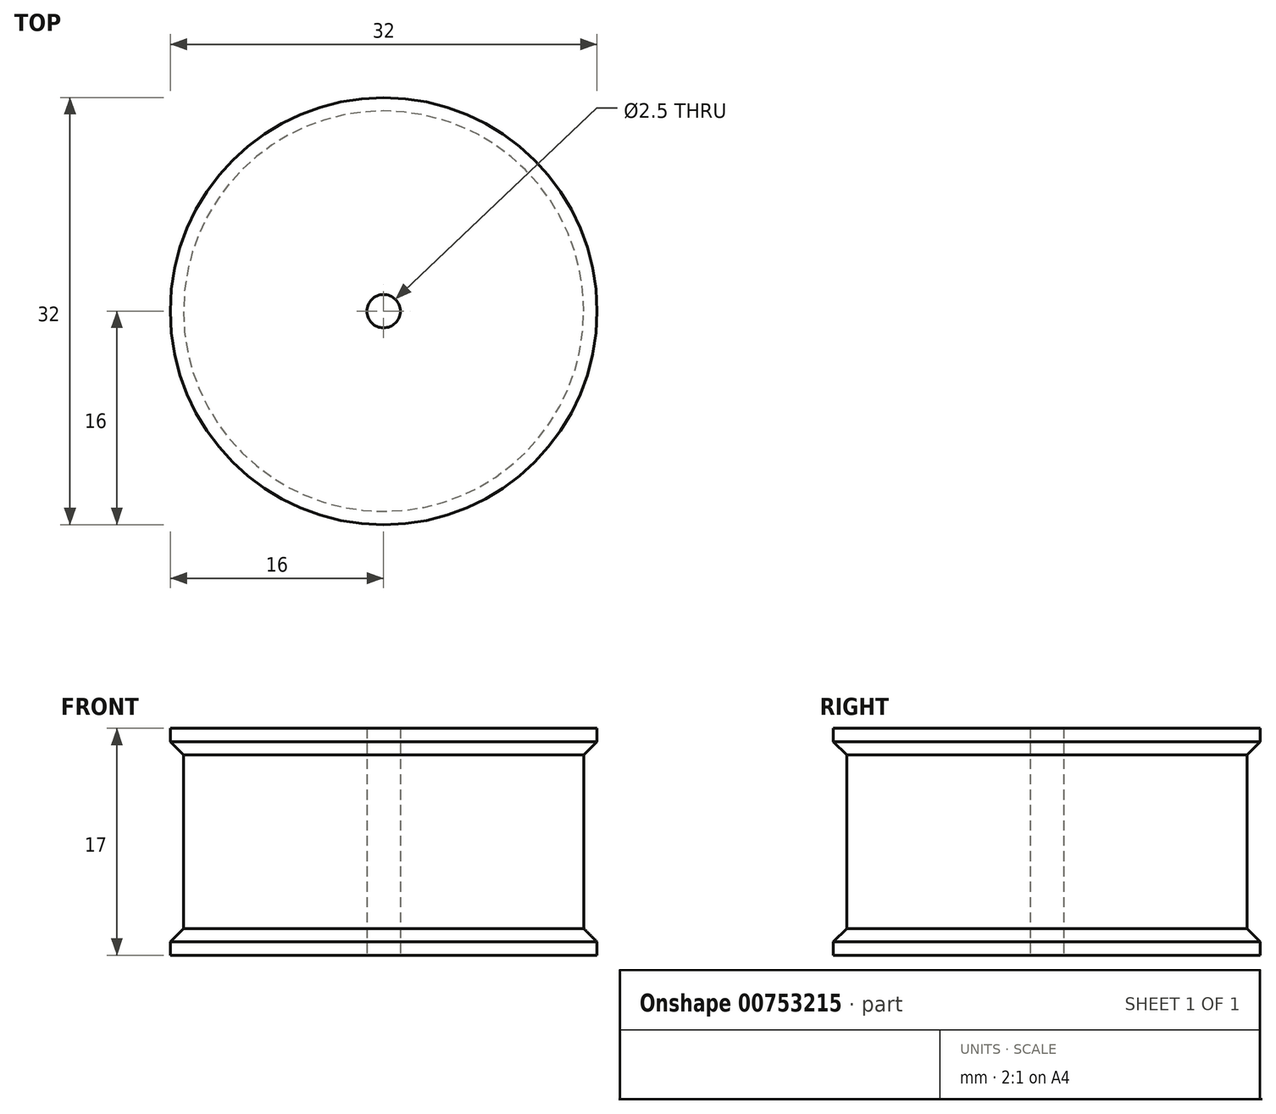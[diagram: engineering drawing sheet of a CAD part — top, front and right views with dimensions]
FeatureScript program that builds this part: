
annotation { "Feature Type Name" : "Feature", "Feature Type Description" : "" }
export const myFeature = defineFeature(function(context is Context, id is Id, definition is map)
    precondition{}
    {
        {
            var Q0;
            Q0=qCreatedBy(makeId("Top.planeOp"),FACE);
            var sketch = newSketch(context, id + "F0", { "sketchPlane" : qUnion([Q0])});
            skCircle(sketch, "E0", {"center": v(0, 0) * mm, "radius": 16 * mm});
            skSolve(sketch);
        }
        {
            var Q0;
            Q0 = qSketchRegion(id + "F0", true);
            extrude(context, id + "F1", {"entities" : qUnion([Q0]), "depth" : 2 * mm, "offsetDistance" : 25 * mm});
        }
        {
            var Q0;
            Q0=makeQuery(id+"F1.opExtrude","CAP_EDGE",EDGE,{"disambiguationData":[OSD([sQuery(id+"F0.wireOp",EDGE,"E0")])],"isStart":false});
            chamfer(context, id + "F2", {"entities" : qUnion([Q0]), "width" : 1 * mm, "tangentPropagation" : true});
        }
        {
            var Q0;
            Q0=qCreatedBy(makeId("Top.planeOp"),FACE);
            var sketch = newSketch(context, id + "F3", { "sketchPlane" : qUnion([Q0])});
            skCircle(sketch, "E1", {"center": v(0, 0) * mm, "radius": 15 * mm});
            skSolve(sketch);
        }
        {
            var Q0;
            Q0=makeQuery(id+"F1.opExtrude","CAP_FACE",FACE,{"disambiguationData":[OSD([sQuery(id+"F0.wireOp",EDGE,"E0")])],"isStart":false});
            var sketch = newSketch(context, id + "F4", { "sketchPlane" : qUnion([Q0])});
            skSolve(sketch);
        }
        {
            var Q0;
            {var subQ0=sQuery(id+"F0.wireOp",EDGE,"E0");Q0=makeQuery(id+"F4.imprint","IMPRINT",FACE,{"disambiguationData":[TD([[makeQuery(id+"F4.imprint","IMPRINT",EDGE,{"derivedFrom":makeQuery(id+"F2.opChamfer","BLEND_EDGE",EDGE,{"blendedFrom":[makeQuery(id+"F1.opExtrude","CAP_EDGE",EDGE,{"disambiguationData":[OSD([subQ0])],"isStart":false}),makeQuery(id+"F1.opExtrude","CAP_FACE",FACE,{"disambiguationData":[OSD([subQ0])],"isStart":false})],"blendedInto":[makeQuery(id+"F1.opExtrude","CAP_FACE",FACE,{"disambiguationData":[OSD([subQ0])],"isStart":false})]})}),1.0]])]});}
            extrude(context, id + "F5", {"entities" : qUnion([Q0]), "operationType" : NewBodyOperationType.ADD, "depth" : 13 * mm, "offsetDistance" : 25 * mm});
        }
        {
            var Q0;
            Q0=makeQuery(id+"F5.opExtrude","CAP_FACE",FACE,{"disambiguationData":[OSD([sQuery(id+"F0.wireOp",EDGE,"E0")])],"isStart":false});
            var sketch = newSketch(context, id + "F6", { "sketchPlane" : qUnion([Q0])});
            skCircle(sketch, "E2", {"center": v(0, 0) * mm, "radius": 16 * mm});
            skSolve(sketch);
        }
        {
            var Q0;
            Q0 = qSketchRegion(id + "F6", true);
            extrude(context, id + "F7", {"entities" : qUnion([Q0]), "operationType" : NewBodyOperationType.ADD, "depth" : 1 * mm, "offsetDistance" : 25 * mm});
        }
        {
            var Q0;
            Q0=makeQuery(id+"F7.opExtrude","CAP_EDGE",EDGE,{"disambiguationData":[OSD([sQuery(id+"F6.wireOp",EDGE,"E2")])],"isStart":true});
            chamfer(context, id + "F8", {"entities" : qUnion([Q0]), "width" : 1 * mm, "tangentPropagation" : true});
        }
        {
            var Q0;
            Q0=makeQuery(id+"F7.opExtrude","CAP_FACE",FACE,{"disambiguationData":[OSD([sQuery(id+"F6.wireOp",EDGE,"E2")])],"isStart":false});
            extrude(context, id + "F9", {"entities" : qUnion([Q0]), "operationType" : NewBodyOperationType.ADD, "depth" : 1 * mm, "offsetDistance" : 25 * mm});
        }
        {
            var Q0;
            Q0=makeQuery(id+"F3.imprint","IMPRINT",FACE,{"disambiguationData":[TD([[makeQuery(id+"F3.imprint","IMPRINT",EDGE,{"derivedFrom":sQuery(id+"F3.wireOp",EDGE,"E1")}),1.0]])]});
            var sketch = newSketch(context, id + "F10", { "sketchPlane" : qUnion([Q0])});
            skCircle(sketch, "E3", {"center": v(0, 0) * mm, "radius": 1.25 * mm});
            skSolve(sketch);
        }
        {
            var Q0;
            Q0=makeQuery(id+"F10.imprint","IMPRINT",FACE,{"disambiguationData":[TD([[makeQuery(id+"F10.imprint","IMPRINT",EDGE,{"derivedFrom":sQuery(id+"F10.wireOp",EDGE,"E3")}),1.0]])]});
            extrude(context, id + "F11", {"entities" : qUnion([Q0]), "operationType" : NewBodyOperationType.REMOVE, "oppositeDirection" : true, "depth" : 2.5 * mm, "offsetDistance" : 25 * mm});
        }
        {
            var Q0;
            Q0=sQuery(id+"F3.wireOp",VERTEX,"E1.center");
            var Q1;
            Q1=makeQuery(id+"F1.opExtrude","SWEPT_BODY",BODY,{"disambiguationData":[OSD([sQuery(id+"F0.wireOp",EDGE,"E0")])]});
            hole(context, id + "F12", {"style" : HoleStyle.SIMPLE, "endStyle" : HoleEndStyle.THROUGH, "oppositeDirection" : true, "holeDiameter" : 2.5 * mm, "majorDiameter" : 5 * mm, "isTappedThrough" : true, "tappedDepth" : 12 * mm, "tapClearance" : 3, "locations" : qUnion([Q0]), "scope" : qUnion([Q1])});
        }
    });
